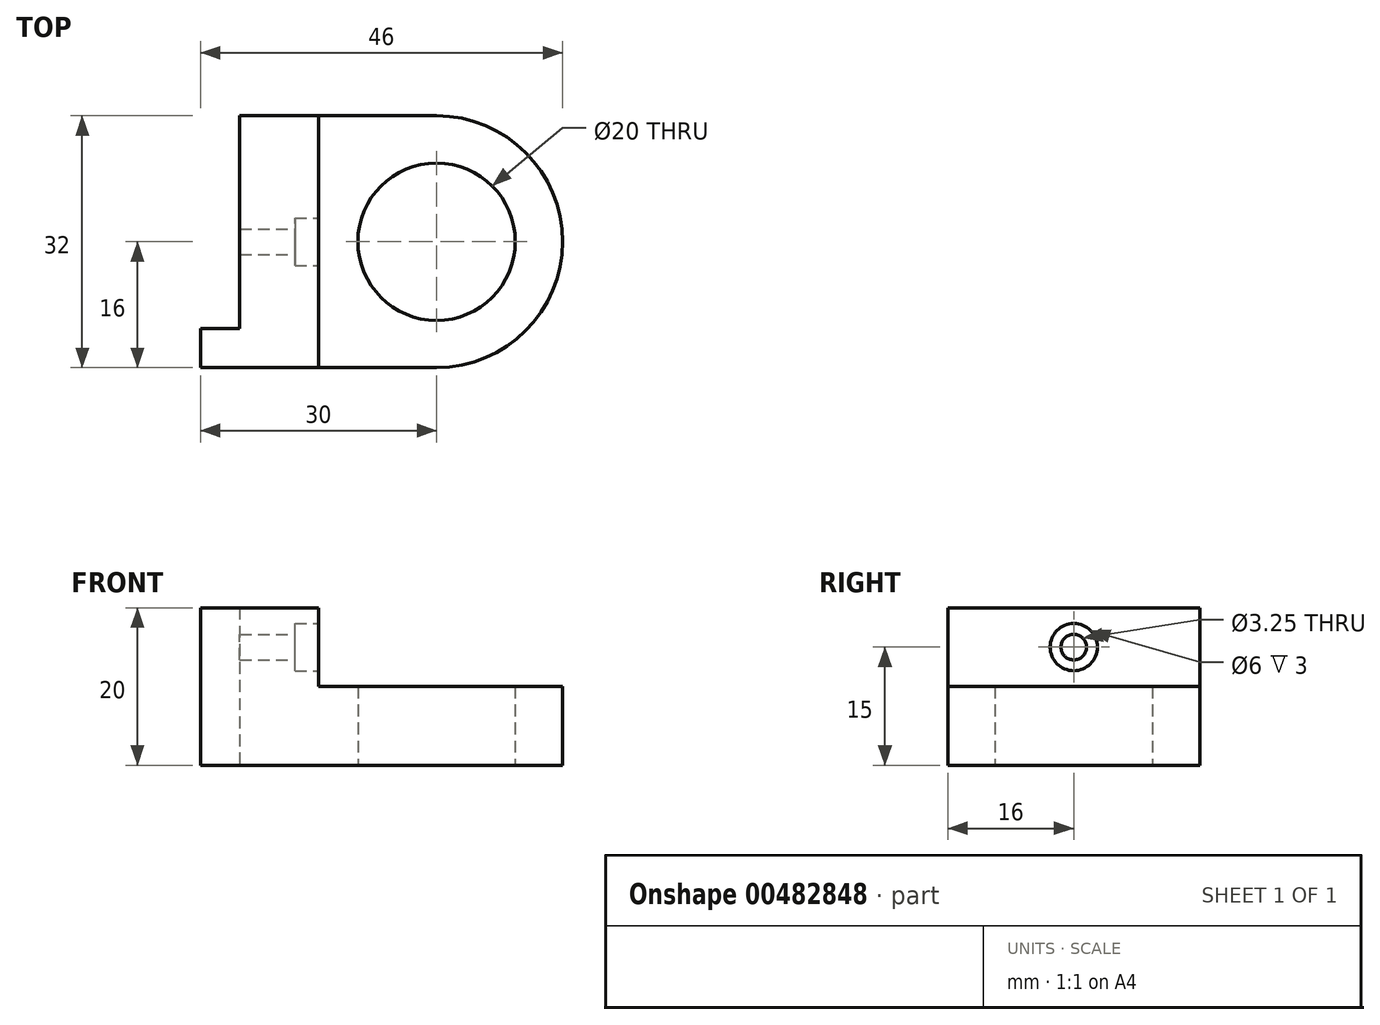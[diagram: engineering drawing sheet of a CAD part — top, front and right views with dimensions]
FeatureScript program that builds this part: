
annotation { "Feature Type Name" : "Feature", "Feature Type Description" : "" }
export const myFeature = defineFeature(function(context is Context, id is Id, definition is map)
    precondition{}
    {
        {
            var Q0;
            Q0=qCreatedBy(makeId("Top.planeOp"),FACE);
            var sketch = newSketch(context, id + "F0", { "sketchPlane" : qUnion([Q0])});
            skCircle(sketch, "E0", {"center": v(0, 0) * mm, "radius": 10 * mm});
            skArc(sketch, "E1", {"start": v(0, -16) * mm, "mid": v(16, 0) * mm, "end": v(0, 16) * mm});
            skLineSegment(sketch, "E2", {"start": v(0, 16) * mm, "end": v(-25, 16) * mm});
            skLineSegment(sketch, "E3", {"start": v(-25, 16) * mm, "end": v(-25, -16) * mm});
            skLineSegment(sketch, "E4", {"start": v(0, -16) * mm, "end": v(-25, -16) * mm});
            skSolve(sketch);
        }
        {
            var Q0;
            Q0 = qSketchRegion(id + "F0", true);
            extrude(context, id + "F1", {"entities" : qUnion([Q0]), "depth" : 10 * mm});
        }
        {
            var Q0;
            Q0=makeQuery(id+"F1.opExtrude","SWEPT_FACE",FACE,{"disambiguationData":[OSD([sQuery(id+"F0.wireOp",EDGE,"E3")])]});
            var sketch = newSketch(context, id + "F2", { "sketchPlane" : qUnion([Q0])});
            skLineSegment(sketch, "E5.0", {"start": v(-16, 10) * mm, "end": v(16, 10) * mm});
            skLineSegment(sketch, "E6", {"start": v(-16, 10) * mm, "end": v(-16, 20) * mm});
            skLineSegment(sketch, "E7", {"start": v(-16, 20) * mm, "end": v(16, 20) * mm});
            skLineSegment(sketch, "E8", {"start": v(16, 20) * mm, "end": v(16, 10) * mm});
            skSolve(sketch);
        }
        {
            var Q0;
            Q0=makeQuery(id+"F2.imprint","IMPRINT",FACE,{"disambiguationData":[TD([[makeQuery(id+"F2.imprint","IMPRINT",EDGE,{"derivedFrom":sQuery(id+"F2.wireOp",EDGE,"E5.0")}),1.0]])]});
            extrude(context, id + "F3", {"entities" : qUnion([Q0]), "operationType" : NewBodyOperationType.ADD, "oppositeDirection" : true, "depth" : 10 * mm});
        }
        {
            var Q0;
            Q0=makeQuery(id+"F3.opExtrude","CAP_FACE",FACE,{"disambiguationData":[OSD([sQuery(id+"F2.wireOp",EDGE,"E5.0"),sQuery(id+"F2.wireOp",EDGE,"E6"),sQuery(id+"F2.wireOp",EDGE,"E7"),sQuery(id+"F2.wireOp",EDGE,"E8")])],"isStart":false});
            var sketch = newSketch(context, id + "F4", { "sketchPlane" : qUnion([Q0])});
            skCircle(sketch, "E9", {"center": v(0, 15) * mm, "radius": 1.63 * mm});
            skSolve(sketch);
        }
        {
            var Q0;
            Q0=makeQuery(id+"F4.imprint","IMPRINT",FACE,{"disambiguationData":[TD([[makeQuery(id+"F4.imprint","IMPRINT",EDGE,{"derivedFrom":sQuery(id+"F4.wireOp",EDGE,"E9")}),1.0]])]});
            extrude(context, id + "F5", {"entities" : qUnion([Q0]), "operationType" : NewBodyOperationType.REMOVE, "oppositeDirection" : true, "depth" : 25 * mm});
        }
        {
            var Q0;
            Q0=makeQuery(id+"F3.opExtrude","CAP_FACE",FACE,{"disambiguationData":[OSD([sQuery(id+"F2.wireOp",EDGE,"E5.0"),sQuery(id+"F2.wireOp",EDGE,"E6"),sQuery(id+"F2.wireOp",EDGE,"E7"),sQuery(id+"F2.wireOp",EDGE,"E8")])],"isStart":false});
            var sketch = newSketch(context, id + "F6", { "sketchPlane" : qUnion([Q0])});
            skCircle(sketch, "E10", {"center": v(0, 15) * mm, "radius": 3 * mm});
            skSolve(sketch);
        }
        {
            var Q0;
            Q0=makeQuery(id+"F6.imprint","IMPRINT",FACE,{"disambiguationData":[TD([[makeQuery(id+"F6.imprint","IMPRINT",EDGE,{"derivedFrom":sQuery(id+"F6.wireOp",EDGE,"E10")}),1.0]])]});
            extrude(context, id + "F7", {"entities" : qUnion([Q0]), "operationType" : NewBodyOperationType.REMOVE, "oppositeDirection" : true, "depth" : 3 * mm});
        }
        {
            var Q0;
            Q0=makeQuery(id+"F3.boolean.opBoolean","MERGE",FACE,{"derivedFrom":[makeQuery(id+"F1.opExtrude","SWEPT_FACE",FACE,{"disambiguationData":[OSD([sQuery(id+"F0.wireOp",EDGE,"E3")])]}),makeQuery(id+"F3.opExtrude","CAP_FACE",FACE,{"disambiguationData":[OSD([sQuery(id+"F2.wireOp",EDGE,"E5.0"),sQuery(id+"F2.wireOp",EDGE,"E6"),sQuery(id+"F2.wireOp",EDGE,"E7"),sQuery(id+"F2.wireOp",EDGE,"E8")])],"isStart":true})]});
            var sketch = newSketch(context, id + "F8", { "sketchPlane" : qUnion([Q0])});
            skLineSegment(sketch, "E11.0", {"start": v(11, 20) * mm, "end": v(16, 20) * mm});
            skLineSegment(sketch, "E12.0", {"start": v(11, 0) * mm, "end": v(16, 0) * mm});
            skLineSegment(sketch, "E13", {"start": v(11, 20) * mm, "end": v(11, 0) * mm});
            skPoint(sketch, "E14.orphan", {"position": v(-16, 20) * mm});
            skPoint(sketch, "E15.orphan", {"position": v(-16, 0) * mm});
            skLineSegment(sketch, "E16", {"start": v(16, 20) * mm, "end": v(16, 0) * mm});
            skPoint(sketch, "E17.0.start.orphan", {"position": v(16, 20) * mm});
            skPoint(sketch, "E18.orphan", {"position": v(16, 0) * mm});
            skSolve(sketch);
        }
        {
            var Q0;
            Q0=makeQuery(id+"F8.imprint","IMPRINT",FACE,{"disambiguationData":[TD([[makeQuery(id+"F8.imprint","IMPRINT",EDGE,{"derivedFrom":sQuery(id+"F8.wireOp",EDGE,"E11.0")}),-1.0]])]});
            extrude(context, id + "F9", {"entities" : qUnion([Q0]), "operationType" : NewBodyOperationType.ADD, "depth" : 5 * mm});
        }
    });
